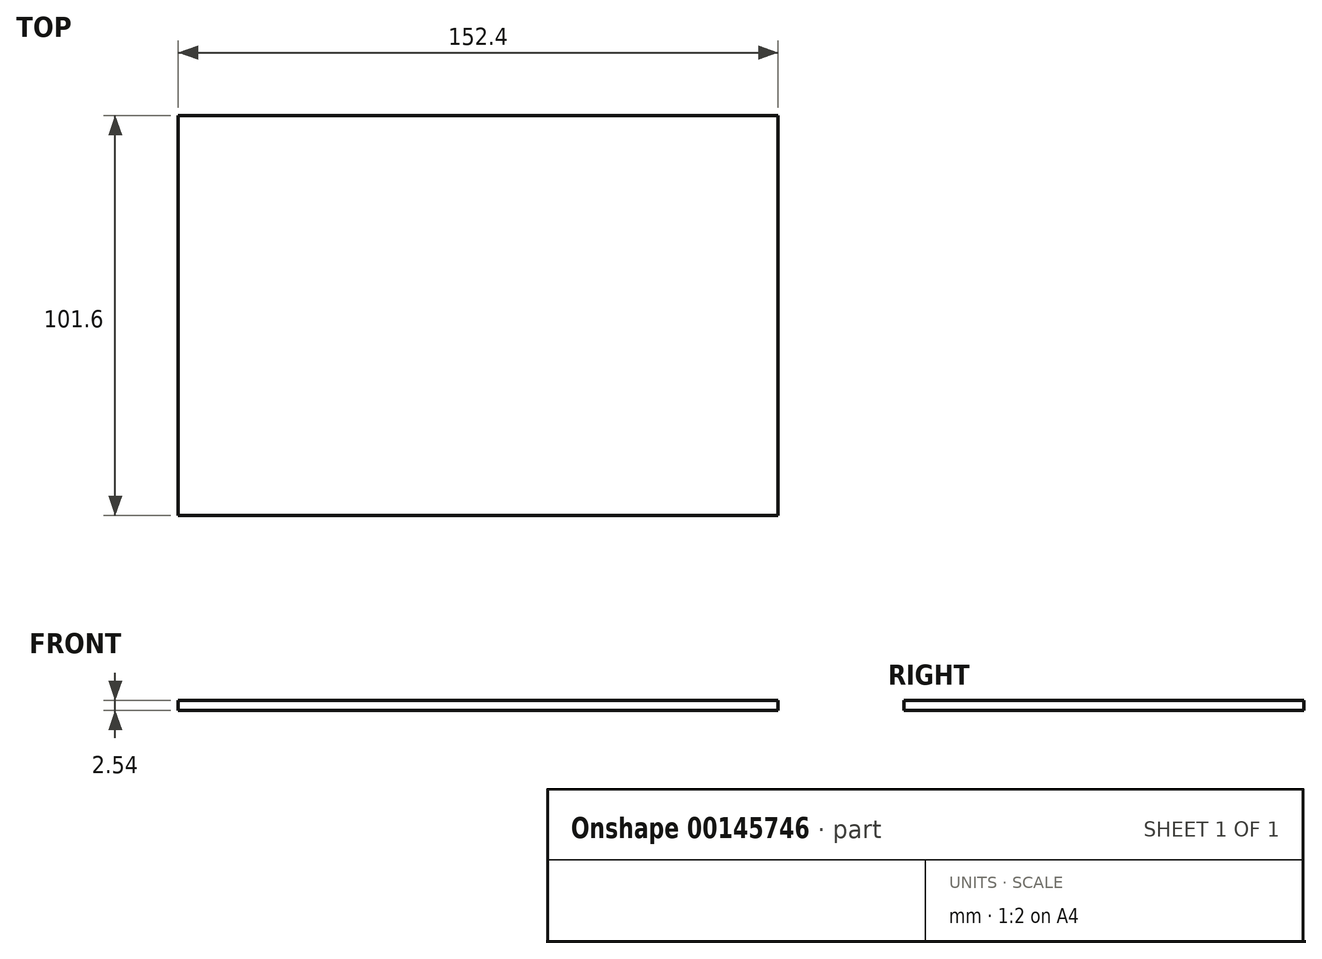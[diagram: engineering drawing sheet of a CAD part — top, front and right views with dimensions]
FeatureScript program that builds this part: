
annotation { "Feature Type Name" : "Feature", "Feature Type Description" : "" }
export const myFeature = defineFeature(function(context is Context, id is Id, definition is map)
    precondition{}
    {
        {
            var Q0;
            Q0=qCreatedBy(makeId("Front.planeOp"),FACE);
            var sketch = newSketch(context, id + "F0", { "sketchPlane" : qUnion([Q0])});
            skLineSegment(sketch, "E0.bottom", {"start": v(-75.07, 3.84) * mm, "end": v(77.33, 3.84) * mm});
            skLineSegment(sketch, "E0.top", {"start": v(-75.07, 1.3) * mm, "end": v(77.33, 1.3) * mm});
            skLineSegment(sketch, "E0.left", {"start": v(-75.07, 3.84) * mm, "end": v(-75.07, 1.3) * mm});
            skLineSegment(sketch, "E0.right", {"start": v(77.33, 3.84) * mm, "end": v(77.33, 1.3) * mm});
            skSolve(sketch);
        }
        {
            var Q0;
            Q0 = qSketchRegion(id + "F0", true);
            extrude(context, id + "F1", {"entities" : qUnion([Q0]), "depth" : 101.6 * mm});
        }
    });
